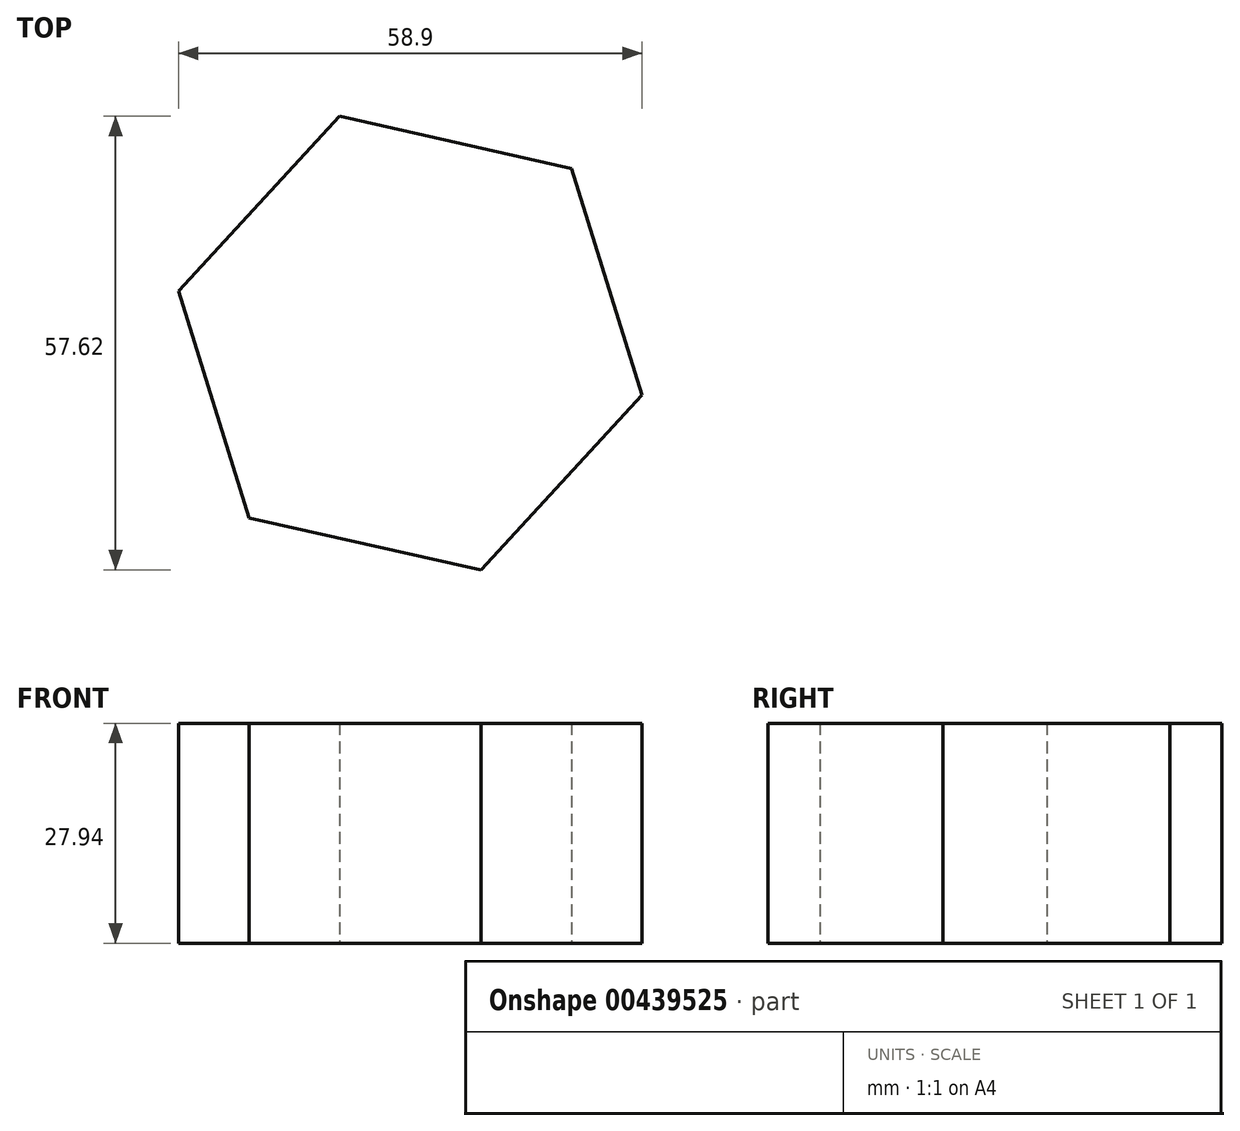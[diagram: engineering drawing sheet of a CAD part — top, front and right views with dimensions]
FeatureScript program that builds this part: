
annotation { "Feature Type Name" : "Feature", "Feature Type Description" : "" }
export const myFeature = defineFeature(function(context is Context, id is Id, definition is map)
    precondition{}
    {
        {
            var Q0;
            Q0=qCreatedBy(makeId("Top.planeOp"),FACE);
            var sketch = newSketch(context, id + "F0", { "sketchPlane" : qUnion([Q0])});
            skCircle(sketch, "E0.cCircle", {"center": v(0, 10.28) * mm, "radius": 26.14 * mm, "construction": true});
            skLineSegment(sketch, "E0.0", {"start": v(29.45, 3.66) * mm, "end": v(9, -18.53) * mm});
            skLineSegment(sketch, "E0.1", {"start": v(9, -18.53) * mm, "end": v(-20.45, -11.92) * mm});
            skLineSegment(sketch, "E0.2", {"start": v(-20.45, -11.92) * mm, "end": v(-29.45, 16.9) * mm});
            skLineSegment(sketch, "E0.3", {"start": v(-29.45, 16.9) * mm, "end": v(-9, 39.09) * mm});
            skLineSegment(sketch, "E0.4", {"start": v(-9, 39.09) * mm, "end": v(20.45, 32.47) * mm});
            skLineSegment(sketch, "E0.5", {"start": v(20.45, 32.47) * mm, "end": v(29.45, 3.66) * mm});
            skPoint(sketch, "E0.0.midPoint", {"position": v(19.22, -7.43) * mm});
            skSolve(sketch);
        }
        {
            var Q0;
            Q0=makeQuery(id+"F0.imprint","IMPRINT",FACE,{"disambiguationData":[TD([[makeQuery(id+"F0.imprint","IMPRINT",EDGE,{"derivedFrom":sQuery(id+"F0.wireOp",EDGE,"E0.0")}),-1.0]])]});
            extrude(context, id + "F1", {"entities" : qUnion([Q0]), "depth" : 27.94 * mm});
        }
    });
